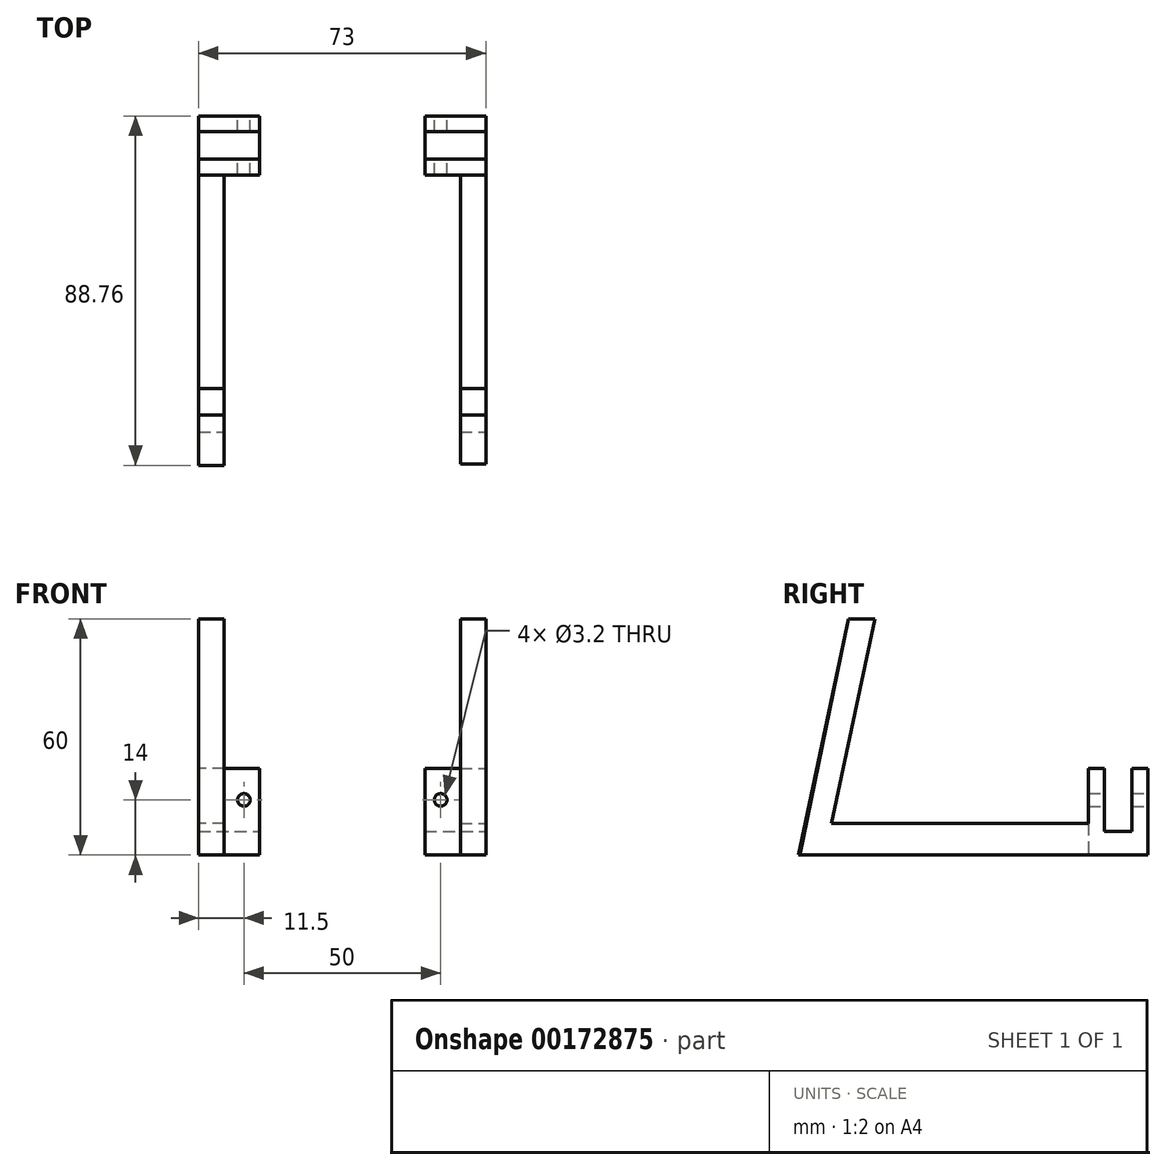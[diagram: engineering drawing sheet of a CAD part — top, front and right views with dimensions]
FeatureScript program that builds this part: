
annotation { "Feature Type Name" : "Feature", "Feature Type Description" : "" }
export const myFeature = defineFeature(function(context is Context, id is Id, definition is map)
    precondition{}
    {
        {
            var Q0;
            Q0=qCreatedBy(makeId("Top.planeOp"),FACE);
            var sketch = newSketch(context, id + "F0", { "sketchPlane" : qUnion([Q0])});
            skLineSegment(sketch, "E0", {"start": v(-30, 50.9) * mm, "end": v(-36.5, 50.9) * mm});
            skLineSegment(sketch, "E1", {"start": v(-36.5, 50.9) * mm, "end": v(-36.5, -31.1) * mm});
            skLineSegment(sketch, "E2", {"start": v(-36.5, -31.1) * mm, "end": v(-30, -31.1) * mm});
            skLineSegment(sketch, "E3", {"start": v(-30, 50.9) * mm, "end": v(-21, 50.9) * mm});
            skLineSegment(sketch, "E4", {"start": v(-21, 50.9) * mm, "end": v(-21, 35.9) * mm});
            skLineSegment(sketch, "E5", {"start": v(-21, 35.9) * mm, "end": v(-30, 35.9) * mm});
            skLineSegment(sketch, "E6", {"start": v(-30, 35.9) * mm, "end": v(-30, -31.1) * mm});
            skLineSegment(sketch, "E7", {"start": v(-36.5, 46.9) * mm, "end": v(-21, 46.9) * mm});
            skLineSegment(sketch, "E8", {"start": v(-21, 46.9) * mm, "end": v(-21, 39.9) * mm});
            skLineSegment(sketch, "E9", {"start": v(-21, 39.9) * mm, "end": v(-36.5, 39.9) * mm});
            skLineSegment(sketch, "E10", {"start": v(-36.5, 39.9) * mm, "end": v(-36.5, 46.9) * mm});
            skLineSegment(sketch, "E11", {"start": v(-36.5, -25.1) * mm, "end": v(-30, -25.1) * mm});
            skLineSegment(sketch, "E12", {"start": v(-30, 35.9) * mm, "end": v(-36.5, 35.9) * mm});
            skLineSegment(sketch, "E13.MirrorCS", {"start": v(36.5, -31.1) * mm, "end": v(30, -31.1) * mm});
            skLineSegment(sketch, "E14.MirrorCS", {"start": v(21, 50.9) * mm, "end": v(21, 35.9) * mm});
            skLineSegment(sketch, "E15.MirrorCS", {"start": v(21, 39.9) * mm, "end": v(36.5, 39.9) * mm});
            skLineSegment(sketch, "E16.MirrorCS", {"start": v(30, 50.9) * mm, "end": v(36.5, 50.9) * mm});
            skLineSegment(sketch, "E17.MirrorCS", {"start": v(36.5, -25.1) * mm, "end": v(30, -25.1) * mm});
            skLineSegment(sketch, "E18.MirrorCS", {"start": v(30, 35.9) * mm, "end": v(36.5, 35.9) * mm});
            skLineSegment(sketch, "E19.MirrorCS", {"start": v(30, 35.9) * mm, "end": v(30, -31.1) * mm});
            skLineSegment(sketch, "E20.MirrorCS", {"start": v(36.5, 50.9) * mm, "end": v(36.5, -31.1) * mm});
            skLineSegment(sketch, "E21.MirrorCS", {"start": v(21, 35.9) * mm, "end": v(30, 35.9) * mm});
            skLineSegment(sketch, "E22.MirrorCS", {"start": v(36.5, 46.9) * mm, "end": v(21, 46.9) * mm});
            skLineSegment(sketch, "E23.MirrorCS", {"start": v(21, 46.9) * mm, "end": v(21, 39.9) * mm});
            skLineSegment(sketch, "E24.MirrorCS", {"start": v(36.5, 39.9) * mm, "end": v(36.5, 46.9) * mm});
            skLineSegment(sketch, "E25.MirrorCS", {"start": v(30, 50.9) * mm, "end": v(21, 50.9) * mm});
            skLineSegment(sketch, "E26", {"start": v(-36.5, 39.9) * mm, "end": v(-36.5, 35.9) * mm});
            skLineSegment(sketch, "E27", {"start": v(-36.5, 50.9) * mm, "end": v(-36.5, 46.9) * mm});
            skSolve(sketch);
        }
        {
            var Q0;
            Q0=makeQuery(id+"F0.imprint","IMPRINT",FACE,{"disambiguationData":[TD([[makeQuery(id+"F0.imprint","IMPRINT",EDGE,{"derivedFrom":sQuery(id+"F0.wireOp",EDGE,"E7")}),-1.0]])]});
            extrude(context, id + "F1", {"entities" : qUnion([Q0]), "depth" : 6 * mm});
        }
        {
            var Q0;
            {var subQ4=sQuery(id+"F0.wireOp",EDGE,"E0");Q0=makeQuery(id+"F0.imprint","IMPRINT",FACE,{"disambiguationData":[TD([[makeQuery(id+"F0.imprint","IMPRINT",EDGE,{"derivedFrom":subQ4}),1.0]])]});}
            var Q1;
            {var subQ1=sQuery(id+"F0.wireOp",EDGE,"E5");Q1=makeQuery(id+"F0.imprint","IMPRINT",FACE,{"disambiguationData":[TD([[makeQuery(id+"F0.imprint","IMPRINT",EDGE,{"derivedFrom":subQ1}),-1.0]])]});}
            extrude(context, id + "F2", {"entities" : qUnion([Q0, Q1]), "operationType" : NewBodyOperationType.ADD, "depth" : 22 * mm});
        }
        {
            var Q0;
            {var subQ0=sQuery(id+"F0.wireOp",EDGE,"E11");Q0=makeQuery(id+"F0.imprint","IMPRINT",FACE,{"disambiguationData":[TD([[makeQuery(id+"F0.imprint","IMPRINT",EDGE,{"derivedFrom":subQ0}),1.0]])]});}
            extrude(context, id + "F3", {"entities" : qUnion([Q0]), "operationType" : NewBodyOperationType.ADD, "depth" : 8 * mm});
        }
        {
            var Q0;
            {var subQ2=sQuery(id+"F0.wireOp",EDGE,"E11");Q0=makeQuery(id+"F0.imprint","IMPRINT",FACE,{"disambiguationData":[TD([[makeQuery(id+"F0.imprint","IMPRINT",EDGE,{"derivedFrom":subQ2}),-1.0]])]});}
            extrude(context, id + "F4", {"entities" : qUnion([Q0]), "operationType" : NewBodyOperationType.ADD, "depth" : 60 * mm});
        }
        {
            var Q0;
            Q0=makeQuery(id+"F0.imprint","IMPRINT",FACE,{"disambiguationData":[TD([[makeQuery(id+"F0.imprint","IMPRINT",EDGE,{"derivedFrom":sQuery(id+"F0.wireOp",EDGE,"E15.MirrorCS")}),1.0]])]});
            extrude(context, id + "F5", {"entities" : qUnion([Q0]), "depth" : 6 * mm});
        }
        {
            var Q0;
            {var subQ1=sQuery(id+"F0.wireOp",EDGE,"E16.MirrorCS");Q0=makeQuery(id+"F0.imprint","IMPRINT",FACE,{"disambiguationData":[TD([[makeQuery(id+"F0.imprint","IMPRINT",EDGE,{"derivedFrom":subQ1}),-1.0]])]});}
            var Q1;
            {var subQ1=sQuery(id+"F0.wireOp",EDGE,"E15.MirrorCS");Q1=makeQuery(id+"F0.imprint","IMPRINT",FACE,{"disambiguationData":[TD([[makeQuery(id+"F0.imprint","IMPRINT",EDGE,{"derivedFrom":subQ1}),-1.0]])]});}
            extrude(context, id + "F6", {"entities" : qUnion([Q0, Q1]), "operationType" : NewBodyOperationType.ADD, "depth" : 22 * mm});
        }
        {
            var Q0;
            {var subQ0=sQuery(id+"F0.wireOp",EDGE,"E17.MirrorCS");Q0=makeQuery(id+"F0.imprint","IMPRINT",FACE,{"disambiguationData":[TD([[makeQuery(id+"F0.imprint","IMPRINT",EDGE,{"derivedFrom":subQ0}),-1.0]])]});}
            extrude(context, id + "F7", {"entities" : qUnion([Q0]), "operationType" : NewBodyOperationType.ADD, "depth" : 8 * mm});
        }
        {
            var Q0;
            {var subQ0=sQuery(id+"F0.wireOp",EDGE,"E13.MirrorCS");Q0=makeQuery(id+"F0.imprint","IMPRINT",FACE,{"disambiguationData":[TD([[makeQuery(id+"F0.imprint","IMPRINT",EDGE,{"derivedFrom":subQ0}),-1.0]])]});}
            extrude(context, id + "F8", {"entities" : qUnion([Q0]), "operationType" : NewBodyOperationType.ADD, "depth" : 60 * mm});
        }
        {
            var Q0;
            Q0=makeQuery(id+"F6.opExtrude","SWEPT_FACE",FACE,{"disambiguationData":[OSD([sQuery(id+"F0.wireOp",EDGE,"E16.MirrorCS"),sQuery(id+"F0.wireOp",EDGE,"E25.MirrorCS")])]});
            var sketch = newSketch(context, id + "F9", { "sketchPlane" : qUnion([Q0])});
            skCircle(sketch, "E28", {"center": v(-25, 14) * mm, "radius": 1.6 * mm});
            skCircle(sketch, "E29", {"center": v(25, 14) * mm, "radius": 1.6 * mm});
            skSolve(sketch);
        }
        {
            var Q0;
            Q0=makeQuery(id+"F9.imprint","IMPRINT",FACE,{"disambiguationData":[TD([[makeQuery(id+"F9.imprint","IMPRINT",EDGE,{"derivedFrom":sQuery(id+"F9.wireOp",EDGE,"E28")}),1.0]])]});
            extrude(context, id + "F10", {"entities" : qUnion([Q0]), "operationType" : NewBodyOperationType.REMOVE, "endBound" : BoundingType.THROUGH_ALL, "oppositeDirection" : true, "depth" : 25 * mm});
        }
        {
            var Q0;
            Q0=makeQuery(id+"F9.imprint","IMPRINT",FACE,{"disambiguationData":[TD([[makeQuery(id+"F9.imprint","IMPRINT",EDGE,{"derivedFrom":sQuery(id+"F9.wireOp",EDGE,"E29")}),1.0]])]});
            extrude(context, id + "F11", {"entities" : qUnion([Q0]), "operationType" : NewBodyOperationType.REMOVE, "endBound" : BoundingType.THROUGH_ALL, "oppositeDirection" : true, "depth" : 25 * mm});
        }
        {
            var Q0;
            {var subQ0=sQuery(id+"F0.wireOp",EDGE,"E6");Q0=makeQuery(id+"F4.boolean.opBoolean","MERGE",FACE,{"derivedFrom":[makeQuery(id+"F3.opExtrude","SWEPT_FACE",FACE,{"disambiguationData":[OSD([subQ0])]}),makeQuery(id+"F4.opExtrude","SWEPT_FACE",FACE,{"disambiguationData":[OSD([subQ0])]})]});}
            var sketch = newSketch(context, id + "F12", { "sketchPlane" : qUnion([Q0])});
            skLineSegment(sketch, "E30", {"start": v(-31.1, 60) * mm, "end": v(-43.85, 0) * mm});
            skLineSegment(sketch, "E31", {"start": v(-43.85, 0) * mm, "end": v(-31.1, 0) * mm});
            skLineSegment(sketch, "E32", {"start": v(-31.1, 0) * mm, "end": v(-18.34, 60) * mm});
            skLineSegment(sketch, "E33", {"start": v(-18.34, 60) * mm, "end": v(-25.1, 60) * mm});
            skLineSegment(sketch, "E34", {"start": v(-25.1, 60) * mm, "end": v(-37.85, 0) * mm});
            skLineSegment(sketch, "E35", {"start": v(-25.1, 8) * mm, "end": v(-25.1, 0) * mm});
            skLineSegment(sketch, "E36", {"start": v(-25.1, 8) * mm, "end": v(-29.4, 8) * mm});
            skSolve(sketch);
        }
        {
            var Q0;
            {var subQ0=sQuery(id+"F12.wireOp",EDGE,"E33");Q0=makeQuery(id+"F12.imprint","IMPRINT",FACE,{"disambiguationData":[TD([[makeQuery(id+"F12.imprint","IMPRINT",EDGE,{"derivedFrom":subQ0}),1.0]])]});}
            var Q1;
            {var subQ6=sQuery(id+"F12.wireOp",EDGE,"E32");var subQ7=makeQuery(id+"F12.imprint","INTERSECT",VERTEX,{"derivedFrom":[subQ6,sQuery(id+"F12.wireOp",EDGE,"E36")]});Q1=makeQuery(id+"F12.imprint","IMPRINT",FACE,{"disambiguationData":[TD([[makeQuery(id+"F12.imprint","IMPRINT",EDGE,{"disambiguationData":[TD([[subQ7,-1.0]])],"derivedFrom":subQ6}),1.0]])]});}
            var Q2;
            {var subQ0=sQuery(id+"F12.wireOp",EDGE,"E31");var subQ4=sQuery(id+"F12.wireOp",EDGE,"E34");var subQ5=makeQuery(id+"F12.imprint","INTERSECT",VERTEX,{"derivedFrom":[subQ0,subQ4]});Q2=makeQuery(id+"F12.imprint","IMPRINT",FACE,{"disambiguationData":[TD([[makeQuery(id+"F12.imprint","IMPRINT",EDGE,{"disambiguationData":[TD([[subQ5,1.0]])],"derivedFrom":subQ4}),1.0]])]});}
            var Q3;
            {var subQ5=sQuery(id+"F12.wireOp",EDGE,"E35");Q3=makeQuery(id+"F12.imprint","IMPRINT",FACE,{"disambiguationData":[TD([[makeQuery(id+"F12.imprint","IMPRINT",EDGE,{"derivedFrom":subQ5}),-1.0]])]});}
            extrude(context, id + "F13", {"entities" : qUnion([Q0, Q1, Q2, Q3]), "operationType" : NewBodyOperationType.ADD, "oppositeDirection" : true, "depth" : 6.5 * mm});
        }
        {
            var Q0;
            {var subQ1=sQuery(id+"F0.wireOp",EDGE,"E6");var subQ2=makeQuery(id+"F4.opExtrude","CAP_EDGE",EDGE,{"disambiguationData":[OSD([subQ1])],"isStart":false});Q0=makeQuery(id+"F12.imprint","IMPRINT",FACE,{"disambiguationData":[TD([[makeQuery(id+"F12.imprint","IMPRINT",EDGE,{"derivedFrom":subQ2}),1.0]])]});}
            var Q1;
            {var subQ0=sQuery(id+"F12.wireOp",EDGE,"E30");Q1=makeQuery(id+"F12.imprint","IMPRINT",FACE,{"disambiguationData":[TD([[makeQuery(id+"F12.imprint","IMPRINT",EDGE,{"derivedFrom":subQ0}),1.0]])]});}
            var Q2;
            {var subQ0=sQuery(id+"F12.wireOp",EDGE,"E36");Q2=makeQuery(id+"F12.imprint","IMPRINT",FACE,{"disambiguationData":[TD([[makeQuery(id+"F12.imprint","IMPRINT",EDGE,{"derivedFrom":subQ0}),-1.0]])]});}
            extrude(context, id + "F14", {"entities" : qUnion([Q0, Q1, Q2]), "operationType" : NewBodyOperationType.REMOVE, "oppositeDirection" : true, "depth" : 6.5 * mm});
        }
        {
            var Q0;
            {var subQ0=sQuery(id+"F0.wireOp",EDGE,"E20.MirrorCS");var subQ1=sQuery(id+"F0.wireOp",EDGE,"E24.MirrorCS");Q0=makeQuery(id+"F8.boolean.opBoolean","MERGE",FACE,{"derivedFrom":[makeQuery(id+"F7.boolean.opBoolean","MERGE",FACE,{"derivedFrom":[makeQuery(id+"F6.boolean.opBoolean","MERGE",FACE,{"derivedFrom":[makeQuery(id+"F5.opExtrude","SWEPT_FACE",FACE,{"disambiguationData":[OSD([subQ1])]}),makeQuery(id+"F6.opExtrude","SWEPT_FACE",FACE,{"disambiguationData":[OSD([subQ0]),TDD([makeQuery(id+"F0.imprint","IMPRINT",EDGE,{"disambiguationData":[TD([[makeQuery(id+"F0.imprint","INTERSECT",VERTEX,{"derivedFrom":[sQuery(id+"F0.wireOp",EDGE,"E16.MirrorCS"),subQ0]}),-1.0]])],"derivedFrom":subQ0})])]}),makeQuery(id+"F6.opExtrude","SWEPT_FACE",FACE,{"disambiguationData":[OSD([subQ0]),TDD([makeQuery(id+"F0.imprint","IMPRINT",EDGE,{"disambiguationData":[TD([[makeQuery(id+"F0.imprint","INTERSECT",VERTEX,{"derivedFrom":[sQuery(id+"F0.wireOp",EDGE,"E18.MirrorCS"),subQ0]}),1.0]])],"derivedFrom":subQ0})])]})]}),makeQuery(id+"F7.opExtrude","SWEPT_FACE",FACE,{"disambiguationData":[OSD([subQ0])]})]}),makeQuery(id+"F8.opExtrude","SWEPT_FACE",FACE,{"disambiguationData":[OSD([subQ0])]})]});}
            var sketch = newSketch(context, id + "F15", { "sketchPlane" : qUnion([Q0])});
            skLineSegment(sketch, "E37", {"start": v(-31.1, 60) * mm, "end": v(-43.85, 0) * mm});
            skLineSegment(sketch, "E38", {"start": v(-43.85, 0) * mm, "end": v(-31.1, 0) * mm});
            skLineSegment(sketch, "E39", {"start": v(-31.1, 0) * mm, "end": v(-18.34, 60) * mm});
            skLineSegment(sketch, "E40", {"start": v(-18.34, 60) * mm, "end": v(-25.1, 60) * mm});
            skLineSegment(sketch, "E41", {"start": v(-25.1, 8) * mm, "end": v(-29.4, 8) * mm});
            skLineSegment(sketch, "E42", {"start": v(-25.1, 60) * mm, "end": v(-37.47, 0) * mm});
            skSolve(sketch);
        }
        {
            var Q0;
            {var subQ0=sQuery(id+"F15.wireOp",EDGE,"E40");Q0=makeQuery(id+"F15.imprint","IMPRINT",FACE,{"disambiguationData":[TD([[makeQuery(id+"F15.imprint","IMPRINT",EDGE,{"derivedFrom":subQ0}),1.0]])]});}
            var Q1;
            {var subQ0=sQuery(id+"F15.wireOp",EDGE,"E39");var subQ10=makeQuery(id+"F15.imprint","INTERSECT",VERTEX,{"derivedFrom":[subQ0,sQuery(id+"F15.wireOp",EDGE,"E41")]});Q1=makeQuery(id+"F15.imprint","IMPRINT",FACE,{"disambiguationData":[TD([[makeQuery(id+"F15.imprint","IMPRINT",EDGE,{"disambiguationData":[TD([[subQ10,-1.0]])],"derivedFrom":subQ0}),1.0]])]});}
            var Q2;
            {var subQ0=sQuery(id+"F15.wireOp",EDGE,"E38");var subQ5=sQuery(id+"F15.wireOp",EDGE,"E42");var subQ6=makeQuery(id+"F15.imprint","INTERSECT",VERTEX,{"derivedFrom":[subQ0,subQ5]});Q2=makeQuery(id+"F15.imprint","IMPRINT",FACE,{"disambiguationData":[TD([[makeQuery(id+"F15.imprint","IMPRINT",EDGE,{"disambiguationData":[TD([[subQ6,1.0]])],"derivedFrom":subQ5}),1.0]])]});}
            extrude(context, id + "F16", {"entities" : qUnion([Q0, Q1, Q2]), "operationType" : NewBodyOperationType.ADD, "oppositeDirection" : true, "depth" : 6.5 * mm});
        }
        {
            var Q0;
            {var subQ1=sQuery(id+"F0.wireOp",EDGE,"E20.MirrorCS");var subQ2=makeQuery(id+"F8.opExtrude","CAP_EDGE",EDGE,{"disambiguationData":[OSD([subQ1])],"isStart":false});Q0=makeQuery(id+"F15.imprint","IMPRINT",FACE,{"disambiguationData":[TD([[makeQuery(id+"F15.imprint","IMPRINT",EDGE,{"derivedFrom":subQ2}),1.0]])]});}
            var Q1;
            {var subQ0=sQuery(id+"F15.wireOp",EDGE,"E37");Q1=makeQuery(id+"F15.imprint","IMPRINT",FACE,{"disambiguationData":[TD([[makeQuery(id+"F15.imprint","IMPRINT",EDGE,{"derivedFrom":subQ0}),1.0]])]});}
            var Q2;
            {var subQ0=sQuery(id+"F15.wireOp",EDGE,"E41");Q2=makeQuery(id+"F15.imprint","IMPRINT",FACE,{"disambiguationData":[TD([[makeQuery(id+"F15.imprint","IMPRINT",EDGE,{"derivedFrom":subQ0}),-1.0]])]});}
            extrude(context, id + "F17", {"entities" : qUnion([Q0, Q1, Q2]), "operationType" : NewBodyOperationType.REMOVE, "oppositeDirection" : true, "depth" : 6.5 * mm});
        }
    });
